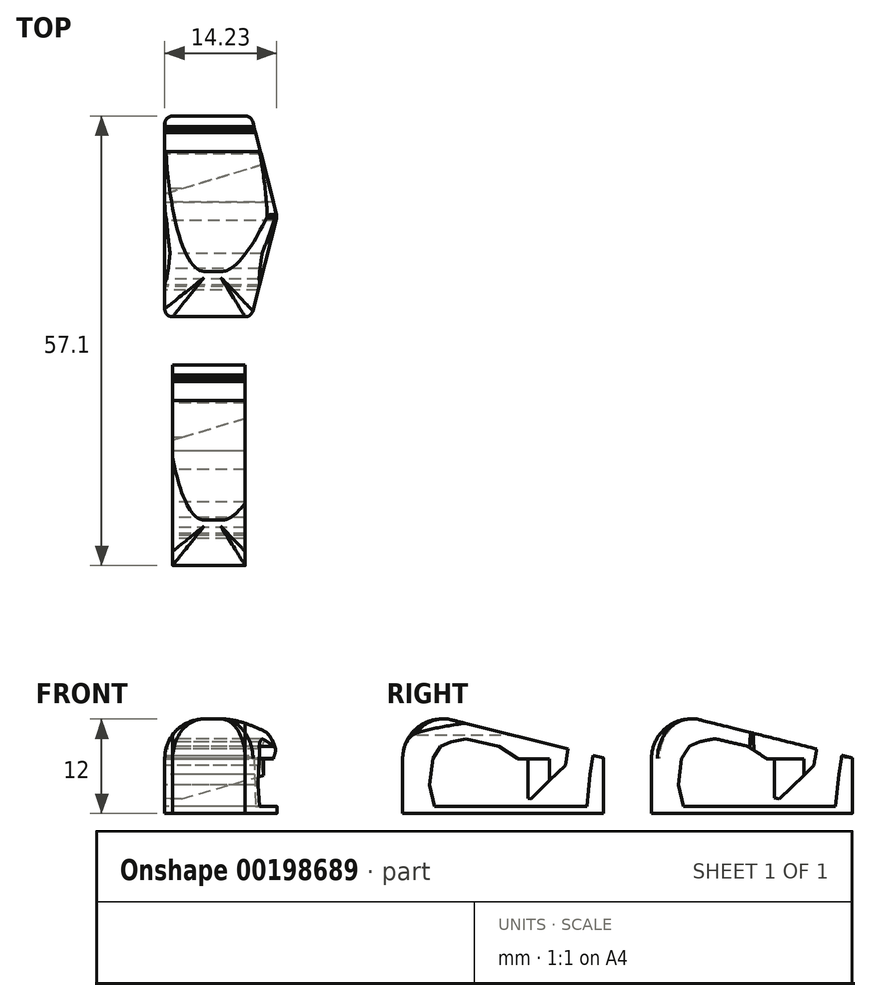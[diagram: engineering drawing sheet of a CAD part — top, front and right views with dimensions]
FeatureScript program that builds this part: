
annotation { "Feature Type Name" : "Feature", "Feature Type Description" : "" }
export const myFeature = defineFeature(function(context is Context, id is Id, definition is map)
    precondition{}
    {
        {
            var Q0;
            Q0=qCreatedBy(makeId("Top.planeOp"),FACE);
            var sketch = newSketch(context, id + "F0", { "sketchPlane" : qUnion([Q0])});
            skLineSegment(sketch, "E0.bottom", {"start": v(-5.5, 12.75) * mm, "end": v(5.5, 12.75) * mm, "construction": true});
            skLineSegment(sketch, "E0.top", {"start": v(-5.5, -12.75) * mm, "end": v(5.5, -12.75) * mm, "construction": true});
            skLineSegment(sketch, "E0.left", {"start": v(-5.5, 12.75) * mm, "end": v(-5.5, -12.75) * mm, "construction": true});
            skLineSegment(sketch, "E0.right", {"start": v(5.5, 12.75) * mm, "end": v(5.5, -12.75) * mm, "construction": true});
            skPoint(sketch, "E0.middle", {"position": v(0, 0) * mm});
            skLineSegment(sketch, "E1", {"start": v(-5.5, 0) * mm, "end": v(8.76, 0) * mm, "construction": true});
            skPoint(sketch, "E1.endSnap0", {"position": v(5.5, 0) * mm});
            skLineSegment(sketch, "E2", {"start": v(-5.5, 11.75) * mm, "end": v(-5.5, -11.75) * mm});
            skLineSegment(sketch, "E3", {"start": v(5.7, -12) * mm, "end": v(8.7, -0.25) * mm});
            skLineSegment(sketch, "E4", {"start": v(8.7, 0.25) * mm, "end": v(5.7, 12) * mm});
            skLineSegment(sketch, "E5", {"start": v(-4.5, 12.75) * mm, "end": v(4.72, 12.75) * mm});
            skPoint(sketch, "E6.visualSharp", {"position": v(-5.5, 12.75) * mm});
            skArc(sketch, "E6.filletArc", {"start": v(-4.5, 12.75) * mm, "mid": v(-5.2, 12.46) * mm, "end": v(-5.5, 11.75) * mm});
            skPoint(sketch, "E7.visualSharp", {"position": v(5.5, 12.75) * mm});
            skArc(sketch, "E7.filletArc", {"start": v(5.7, 12) * mm, "mid": v(5.34, 12.54) * mm, "end": v(4.72, 12.75) * mm});
            skPoint(sketch, "E8.visualSharp", {"position": v(8.76, 0) * mm});
            skArc(sketch, "E8.filletArc", {"start": v(8.7, -0.25) * mm, "mid": v(8.73, 0) * mm, "end": v(8.7, 0.25) * mm});
            skLineSegment(sketch, "E9", {"start": v(-4.5, -12.75) * mm, "end": v(4.72, -12.75) * mm});
            skPoint(sketch, "E10.visualSharp", {"position": v(5.5, -12.75) * mm});
            skArc(sketch, "E10.filletArc", {"start": v(4.72, -12.75) * mm, "mid": v(5.34, -12.54) * mm, "end": v(5.7, -12) * mm});
            skPoint(sketch, "E11.visualSharp", {"position": v(-5.5, -12.75) * mm});
            skArc(sketch, "E11.filletArc", {"start": v(-5.5, -11.75) * mm, "mid": v(-5.2, -12.46) * mm, "end": v(-4.5, -12.75) * mm});
            skSolve(sketch);
        }
        {
            var Q0;
            Q0=makeQuery(id+"F0.imprint","IMPRINT",FACE,{"disambiguationData":[TD([[makeQuery(id+"F0.imprint","IMPRINT",EDGE,{"derivedFrom":sQuery(id+"F0.wireOp",EDGE,"E2")}),1.0]])]});
            extrude(context, id + "F1", {"entities" : qUnion([Q0]), "depth" : 12 * mm});
        }
        {
            var Q0;
            Q0=makeQuery(id+"F1.opExtrude","CAP_EDGE",EDGE,{"disambiguationData":[OSD([sQuery(id+"F0.wireOp",EDGE,"E2")])],"isStart":false});
            fillet(context, id + "F2", {"entities" : qUnion([Q0]), "radius" : 5 * mm, "tangentPropagation" : true, "allowEdgeOverflow" : false});
        }
        {
            var Q0;
            Q0=qCreatedBy(makeId("Right.planeOp"),FACE);
            var sketch = newSketch(context, id + "F3", { "sketchPlane" : qUnion([Q0])});
            skLineSegment(sketch, "E12", {"start": v(-8.75, 12.44) * mm, "end": v(16.08, 6.22) * mm});
            skLineSegment(sketch, "E13", {"start": v(16.08, 6.22) * mm, "end": v(13.81, 14.06) * mm});
            skLineSegment(sketch, "E14", {"start": v(13.81, 14.06) * mm, "end": v(-8.75, 12.44) * mm});
            skSolve(sketch);
        }
        {
            var Q0;
            Q0=makeQuery(id+"F3.imprint","IMPRINT",FACE,{"disambiguationData":[TD([[makeQuery(id+"F3.imprint","IMPRINT",EDGE,{"derivedFrom":sQuery(id+"F3.wireOp",EDGE,"E12")}),1.0]])]});
            extrude(context, id + "F4", {"entities" : qUnion([Q0]), "operationType" : NewBodyOperationType.REMOVE, "endBound" : BoundingType.SYMMETRIC, "oppositeDirection" : true, "depth" : 15.8 * mm});
        }
        {
            var Q0;
            Q0=makeQuery(id+"F1.opExtrude","SWEPT_FACE",FACE,{"disambiguationData":[OSD([sQuery(id+"F0.wireOp",EDGE,"E2")])]});
            var sketch = newSketch(context, id + "F5", { "sketchPlane" : qUnion([Q0])});
            skLineSegment(sketch, "E15", {"start": v(0, 0) * mm, "end": v(0, 7) * mm, "construction": true});
            skLineSegment(sketch, "E16.bottom", {"start": v(-10.63, 6.09) * mm, "end": v(10.63, 6.09) * mm, "construction": true});
            skLineSegment(sketch, "E16.top", {"start": v(-10.63, 0.91) * mm, "end": v(10.63, 0.91) * mm, "construction": true});
            skLineSegment(sketch, "E16.left", {"start": v(-10.63, 6.09) * mm, "end": v(-10.63, 0.91) * mm, "construction": true});
            skLineSegment(sketch, "E16.right", {"start": v(10.63, 6.09) * mm, "end": v(10.63, 0.91) * mm, "construction": true});
            skPoint(sketch, "E16.middle", {"position": v(0, 3.5) * mm});
            skLineSegment(sketch, "E17", {"start": v(-10.63, 0.91) * mm, "end": v(8.7, 0.91) * mm});
            skLineSegment(sketch, "E18", {"start": v(8.7, 0.91) * mm, "end": v(9.33, 3.6) * mm});
            skLineSegment(sketch, "E19", {"start": v(9.33, 3.6) * mm, "end": v(8.92, 7) * mm});
            skLineSegment(sketch, "E20", {"start": v(8.92, 7) * mm, "end": v(7.93, 8.54) * mm});
            skLineSegment(sketch, "E21", {"start": v(7.93, 8.54) * mm, "end": v(6.62, 9.12) * mm});
            skLineSegment(sketch, "E22", {"start": v(6.62, 9.12) * mm, "end": v(4.71, 9.5) * mm});
            skLineSegment(sketch, "E23", {"start": v(4.71, 9.5) * mm, "end": v(0.53, 8.54) * mm});
            skLineSegment(sketch, "E24", {"start": v(0.53, 8.54) * mm, "end": v(-1.83, 7) * mm});
            skLineSegment(sketch, "E25", {"start": v(-1.83, 7) * mm, "end": v(-2.47, 2.04) * mm});
            skLineSegment(sketch, "E26", {"start": v(-2.47, 2.04) * mm, "end": v(-3.51, 1.88) * mm});
            skLineSegment(sketch, "E27", {"start": v(-3.51, 1.88) * mm, "end": v(-7.9, 6.09) * mm});
            skLineSegment(sketch, "E28", {"start": v(-7.9, 6.09) * mm, "end": v(-8.46, 9.51) * mm});
            skLineSegment(sketch, "E29", {"start": v(-8.46, 9.51) * mm, "end": v(-11.53, 7.99) * mm});
            skLineSegment(sketch, "E30", {"start": v(-11.53, 7.99) * mm, "end": v(-11.03, 4.95) * mm});
            skLineSegment(sketch, "E31", {"start": v(-11.03, 4.95) * mm, "end": v(-10.63, 0.91) * mm});
            skSolve(sketch);
        }
        {
            var Q0;
            {var subQ0=sQuery(id+"F5.wireOp",EDGE,"E29");Q0=makeQuery(id+"F5.imprint","IMPRINT",FACE,{"disambiguationData":[TD([[makeQuery(id+"F5.imprint","IMPRINT",EDGE,{"derivedFrom":subQ0}),1.0]])]});}
            var Q1;
            Q1=makeQuery(id+"F5.imprint","IMPRINT",FACE,{"disambiguationData":[TD([[makeQuery(id+"F5.imprint","IMPRINT",EDGE,{"derivedFrom":sQuery(id+"F5.wireOp",EDGE,"E17")}),1.0]])]});
            var Q2;
            {var subQ0=sQuery(id+"F5.wireOp",EDGE,"E20");Q2=makeQuery(id+"F5.imprint","IMPRINT",FACE,{"disambiguationData":[TD([[makeQuery(id+"F5.imprint","IMPRINT",EDGE,{"derivedFrom":subQ0}),1.0]])]});}
            extrude(context, id + "F6", {"entities" : qUnion([Q0, Q1, Q2]), "operationType" : NewBodyOperationType.REMOVE, "oppositeDirection" : true, "depth" : 25 * mm});
        }
        {
            var Q0;
            Q0=makeQuery(id+"F6.boolean.opBoolean","COPY",FACE,{"derivedFrom":makeQuery(id+"F6.opExtrude","SWEPT_FACE",FACE,{"disambiguationData":[OSD([sQuery(id+"F5.wireOp",EDGE,"E17")])]})});
            var sketch = newSketch(context, id + "F7", { "sketchPlane" : qUnion([Q0])});
            skLineSegment(sketch, "E32", {"start": v(11.04, 7.8) * mm, "end": v(-8.92, 1.85) * mm});
            skLineSegment(sketch, "E33", {"start": v(-8.92, 1.85) * mm, "end": v(-8.92, -0.9) * mm});
            skLineSegment(sketch, "E34", {"start": v(-8.92, -0.9) * mm, "end": v(12.06, -0.9) * mm});
            skLineSegment(sketch, "E35", {"start": v(12.06, -0.9) * mm, "end": v(11.04, 7.8) * mm});
            skSolve(sketch);
        }
        {
            var Q0;
            {var subQ1=sQuery(id+"F5.wireOp",EDGE,"E17");var subQ6=makeQuery(id+"F6.opExtrude","SWEPT_FACE",FACE,{"disambiguationData":[OSD([subQ1])]});var subQ7=makeQuery(id+"F6.boolean.opBoolean","INTERSECT",EDGE,{"derivedFrom":[makeQuery(id+"F1.opExtrude","SWEPT_FACE",FACE,{"disambiguationData":[OSD([sQuery(id+"F0.wireOp",EDGE,"E8.filletArc")])]}),subQ6]});Q0=makeQuery(id+"F7.imprint","IMPRINT",FACE,{"disambiguationData":[TD([[makeQuery(id+"F7.imprint","IMPRINT",EDGE,{"derivedFrom":subQ7}),-1.0]])]});}
            extrude(context, id + "F8", {"entities" : qUnion([Q0]), "operationType" : NewBodyOperationType.REMOVE, "depth" : 6 * mm});
        }
        {
            var Q0;
            Q0=makeQuery(id+"F1.opExtrude","SWEPT_BODY",BODY,{"disambiguationData":[OSD([sQuery(id+"F0.wireOp",EDGE,"E2"),sQuery(id+"F0.wireOp",EDGE,"E3"),sQuery(id+"F0.wireOp",EDGE,"E4"),sQuery(id+"F0.wireOp",EDGE,"E5"),sQuery(id+"F0.wireOp",EDGE,"E6.filletArc"),sQuery(id+"F0.wireOp",EDGE,"E7.filletArc"),sQuery(id+"F0.wireOp",EDGE,"E8.filletArc"),sQuery(id+"F0.wireOp",EDGE,"E9"),sQuery(id+"F0.wireOp",EDGE,"E10.filletArc"),sQuery(id+"F0.wireOp",EDGE,"E11.filletArc")])]});
            transform(context, id + "F9", {"entities" : qUnion([Q0]), "transformType" : TransformType.TRANSLATION_3D, "dx" : 0 * mm, "dy" : -31.6 * mm, "dz" : 0 * mm, "makeCopy" : true});
        }
        {
            var Q0;
            Q0=makeQuery(id+"F9.opPattern","COPY",FACE,{"derivedFrom":makeQuery(id+"F1.opExtrude","SWEPT_FACE",FACE,{"disambiguationData":[OSD([sQuery(id+"F0.wireOp",EDGE,"E9")])]}),"instanceName":"1"});
            var sketch = newSketch(context, id + "F10", { "sketchPlane" : qUnion([Q0])});
            skLineSegment(sketch, "E36.bottom", {"start": v(-4.5, -0.76) * mm, "end": v(-8.64, -0.76) * mm});
            skLineSegment(sketch, "E36.top", {"start": v(-4.5, 14.07) * mm, "end": v(-8.64, 14.07) * mm});
            skLineSegment(sketch, "E36.left", {"start": v(-4.5, -0.76) * mm, "end": v(-4.5, 14.07) * mm});
            skLineSegment(sketch, "E36.right", {"start": v(-8.64, -0.76) * mm, "end": v(-8.64, 14.07) * mm});
            skLineSegment(sketch, "E37.bottom", {"start": v(4.72, 0) * mm, "end": v(15.79, 0) * mm});
            skLineSegment(sketch, "E37.top", {"start": v(4.72, 13.59) * mm, "end": v(15.79, 13.59) * mm});
            skLineSegment(sketch, "E37.left", {"start": v(4.72, 0) * mm, "end": v(4.72, 13.59) * mm});
            skLineSegment(sketch, "E37.right", {"start": v(15.79, 0) * mm, "end": v(15.79, 13.59) * mm});
            skSolve(sketch);
        }
        {
            var Q0;
            {var subQ5=sQuery(id+"F10.wireOp",EDGE,"E36.bottom");Q0=makeQuery(id+"F10.imprint","IMPRINT",FACE,{"disambiguationData":[TD([[makeQuery(id+"F10.imprint","IMPRINT",EDGE,{"derivedFrom":subQ5}),-1.0]])]});}
            var Q1;
            {var subQ1=sQuery(id+"F10.wireOp",EDGE,"E37.bottom");Q1=makeQuery(id+"F10.imprint","IMPRINT",FACE,{"disambiguationData":[TD([[makeQuery(id+"F10.imprint","IMPRINT",EDGE,{"derivedFrom":subQ1}),1.0]])]});}
            extrude(context, id + "F11", {"entities" : qUnion([Q0, Q1]), "operationType" : NewBodyOperationType.REMOVE, "oppositeDirection" : true, "depth" : 30 * mm});
        }
    });
